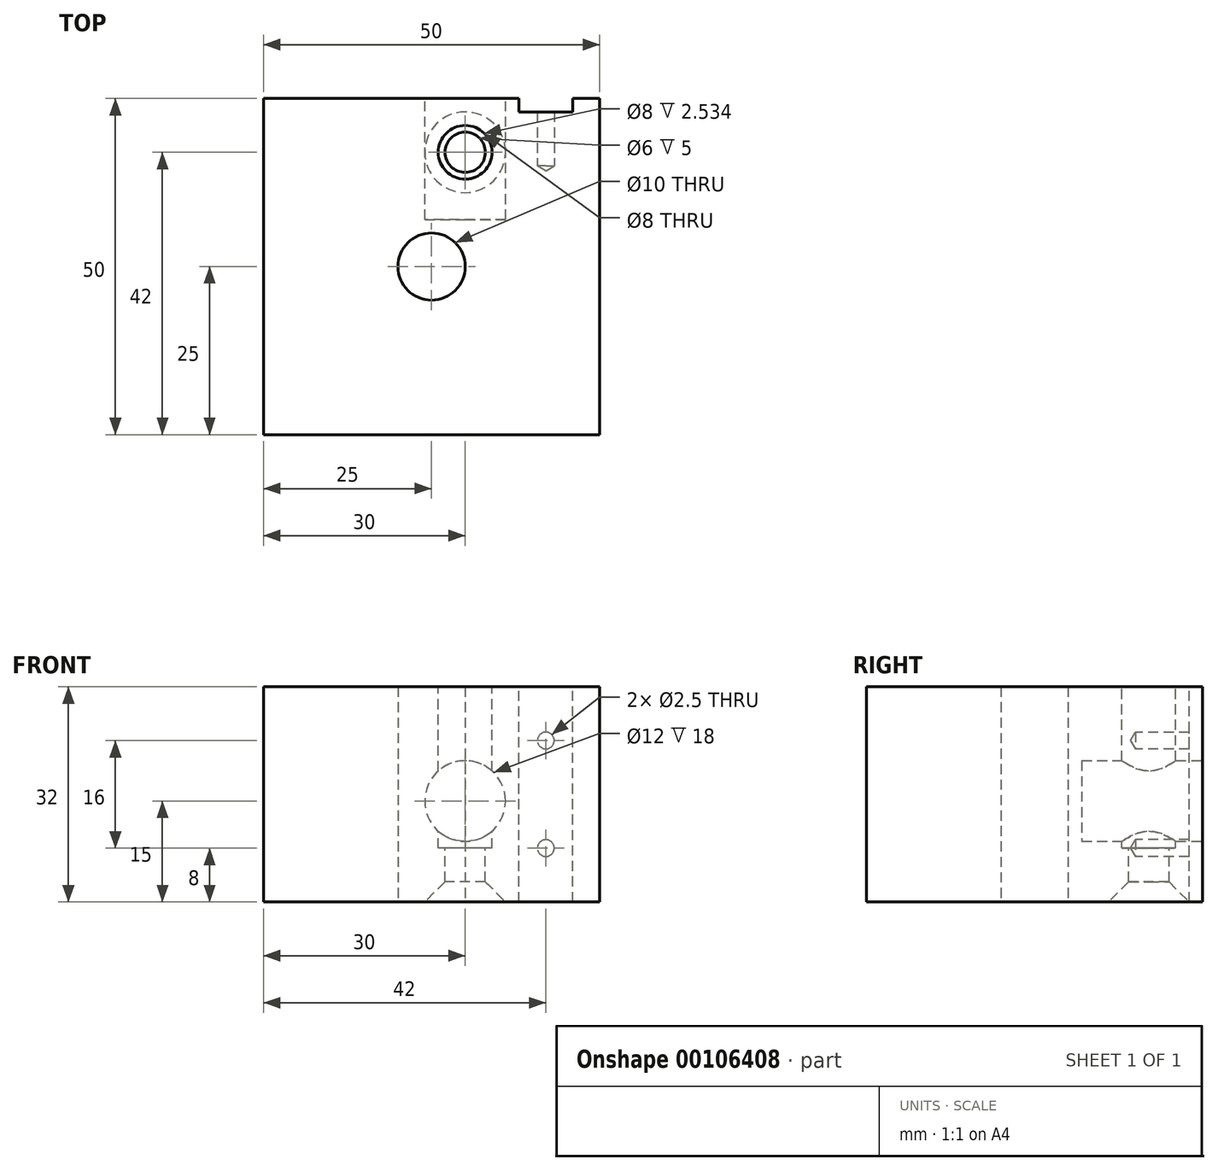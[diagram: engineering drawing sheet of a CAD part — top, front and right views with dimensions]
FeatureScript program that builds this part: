
annotation { "Feature Type Name" : "Feature", "Feature Type Description" : "" }
export const myFeature = defineFeature(function(context is Context, id is Id, definition is map)
    precondition{}
    {
        {
            var Q0;
            Q0=qCreatedBy(makeId("Top.planeOp"),FACE);
            var sketch = newSketch(context, id + "F0", { "sketchPlane" : qUnion([Q0])});
            skLineSegment(sketch, "E0.bottom", {"start": v(25, -25) * mm, "end": v(-25, -25) * mm});
            skLineSegment(sketch, "E0.top", {"start": v(25, 25) * mm, "end": v(-25, 25) * mm});
            skLineSegment(sketch, "E0.left", {"start": v(25, -25) * mm, "end": v(25, 25) * mm});
            skLineSegment(sketch, "E0.right", {"start": v(-25, -25) * mm, "end": v(-25, 25) * mm});
            skPoint(sketch, "E0.middle", {"position": v(0, 0) * mm});
            skCircle(sketch, "E1", {"center": v(0, 0) * mm, "radius": 5 * mm});
            skSolve(sketch);
        }
        {
            var Q0;
            Q0=makeQuery(id+"F0.imprint","IMPRINT",FACE,{"disambiguationData":[TD([[makeQuery(id+"F0.imprint","IMPRINT",EDGE,{"derivedFrom":sQuery(id+"F0.wireOp",EDGE,"E0.bottom")}),-1.0]])]});
            extrude(context, id + "F1", {"entities" : qUnion([Q0]), "depth" : 32 * mm, "symmetric" : true});
        }
        {
            var Q0;
            Q0=makeQuery(id+"F1.opExtrude","CAP_FACE",FACE,{"disambiguationData":[OSD([sQuery(id+"F0.wireOp",EDGE,"E0.bottom"),sQuery(id+"F0.wireOp",EDGE,"E0.top"),sQuery(id+"F0.wireOp",EDGE,"E0.left"),sQuery(id+"F0.wireOp",EDGE,"E0.right"),sQuery(id+"F0.wireOp",EDGE,"E1")])],"isStart":false});
            var sketch = newSketch(context, id + "F2", { "sketchPlane" : qUnion([Q0])});
            skLineSegment(sketch, "E2.bottom", {"start": v(13, 25) * mm, "end": v(21, 25) * mm});
            skLineSegment(sketch, "E2.top", {"start": v(13, 23) * mm, "end": v(21, 23) * mm});
            skLineSegment(sketch, "E2.left", {"start": v(13, 25) * mm, "end": v(13, 23) * mm});
            skLineSegment(sketch, "E2.right", {"start": v(21, 25) * mm, "end": v(21, 23) * mm});
            skSolve(sketch);
        }
        {
            var Q0;
            Q0=makeQuery(id+"F2.imprint","IMPRINT",FACE,{"disambiguationData":[TD([[makeQuery(id+"F2.imprint","IMPRINT",EDGE,{"derivedFrom":sQuery(id+"F2.wireOp",EDGE,"E2.bottom")}),1.0]])]});
            extrude(context, id + "F3", {"entities" : qUnion([Q0]), "operationType" : NewBodyOperationType.REMOVE, "endBound" : BoundingType.THROUGH_ALL, "oppositeDirection" : true, "depth" : 25 * mm});
        }
        {
            var Q0;
            Q0=makeQuery(id+"F1.opExtrude","CAP_FACE",FACE,{"disambiguationData":[OSD([sQuery(id+"F0.wireOp",EDGE,"E0.bottom"),sQuery(id+"F0.wireOp",EDGE,"E0.top"),sQuery(id+"F0.wireOp",EDGE,"E0.left"),sQuery(id+"F0.wireOp",EDGE,"E0.right"),sQuery(id+"F0.wireOp",EDGE,"E1")])],"isStart":false});
            var sketch = newSketch(context, id + "F4", { "sketchPlane" : qUnion([Q0])});
            skCircle(sketch, "E3", {"center": v(5, 17) * mm, "radius": 3 * mm});
            skSolve(sketch);
        }
        {
            var Q0;
            Q0=makeQuery(id+"F4.imprint","IMPRINT",FACE,{"disambiguationData":[TD([[makeQuery(id+"F4.imprint","IMPRINT",EDGE,{"derivedFrom":sQuery(id+"F4.wireOp",EDGE,"E3")}),1.0]])]});
            extrude(context, id + "F5", {"entities" : qUnion([Q0]), "operationType" : NewBodyOperationType.REMOVE, "endBound" : BoundingType.THROUGH_ALL, "oppositeDirection" : true, "depth" : 25 * mm});
        }
        {
            var Q0;
            Q0=makeQuery(id+"F1.opExtrude","CAP_FACE",FACE,{"disambiguationData":[OSD([sQuery(id+"F0.wireOp",EDGE,"E0.bottom"),sQuery(id+"F0.wireOp",EDGE,"E0.top"),sQuery(id+"F0.wireOp",EDGE,"E0.left"),sQuery(id+"F0.wireOp",EDGE,"E0.right"),sQuery(id+"F0.wireOp",EDGE,"E1")])],"isStart":false});
            var sketch = newSketch(context, id + "F6", { "sketchPlane" : qUnion([Q0])});
            skCircle(sketch, "E4", {"center": v(5, 17) * mm, "radius": 4 * mm});
            skSolve(sketch);
        }
        {
            var Q0;
            Q0=makeQuery(id+"F6.imprint","IMPRINT",FACE,{"disambiguationData":[TD([[makeQuery(id+"F6.imprint","IMPRINT",EDGE,{"derivedFrom":sQuery(id+"F6.wireOp",EDGE,"E4")}),1.0]])]});
            extrude(context, id + "F7", {"entities" : qUnion([Q0]), "operationType" : NewBodyOperationType.REMOVE, "oppositeDirection" : true, "depth" : 24 * mm});
        }
        {
            var Q0;
            {var subQ1=sQuery(id+"F0.wireOp",EDGE,"E0.right");var subQ3=sQuery(id+"F0.wireOp",EDGE,"E0.top");Q0=makeQuery(id+"F3.boolean.opBoolean","SPLIT",FACE,{"disambiguationData":[TD([makeQuery(id+"F1.opExtrude","SWEPT_FACE",FACE,{"disambiguationData":[OSD([subQ1])]})])],"derivedFrom":makeQuery(id+"F1.opExtrude","SWEPT_FACE",FACE,{"disambiguationData":[OSD([subQ3])]})});}
            var sketch = newSketch(context, id + "F8", { "sketchPlane" : qUnion([Q0])});
            skCircle(sketch, "E5", {"center": v(-5, -1) * mm, "radius": 6 * mm});
            skSolve(sketch);
        }
        {
            var Q0;
            Q0=makeQuery(id+"F8.imprint","IMPRINT",FACE,{"disambiguationData":[TD([[makeQuery(id+"F8.imprint","IMPRINT",EDGE,{"derivedFrom":sQuery(id+"F8.wireOp",EDGE,"E5")}),1.0]])]});
            extrude(context, id + "F9", {"entities" : qUnion([Q0]), "operationType" : NewBodyOperationType.REMOVE, "oppositeDirection" : true, "depth" : 18 * mm});
        }
        {
            var Q0;
            Q0=makeQuery(id+"F5.boolean.opBoolean","INTERSECT",EDGE,{"derivedFrom":[makeQuery(id+"F1.opExtrude","CAP_FACE",FACE,{"disambiguationData":[OSD([sQuery(id+"F0.wireOp",EDGE,"E0.bottom"),sQuery(id+"F0.wireOp",EDGE,"E0.top"),sQuery(id+"F0.wireOp",EDGE,"E0.left"),sQuery(id+"F0.wireOp",EDGE,"E0.right"),sQuery(id+"F0.wireOp",EDGE,"E1")])],"isStart":true}),makeQuery(id+"F5.opExtrude","SWEPT_FACE",FACE,{"disambiguationData":[OSD([sQuery(id+"F4.wireOp",EDGE,"E3")])]})]});
            chamfer(context, id + "F10", {"entities" : qUnion([Q0]), "chamferType" : ChamferType.OFFSET_ANGLE, "width" : 3 * mm, "oppositeDirection" : false, "angle" : 45 * degree, "tangentPropagation" : true});
        }
        {
            var Q0;
            Q0=makeQuery(id+"F3.boolean.opBoolean","COPY",FACE,{"derivedFrom":makeQuery(id+"F3.opExtrude","SWEPT_FACE",FACE,{"disambiguationData":[OSD([sQuery(id+"F2.wireOp",EDGE,"E2.top")])]})});
            var sketch = newSketch(context, id + "F11", { "sketchPlane" : qUnion([Q0])});
            skPoint(sketch, "E6", {"position": v(-17, 8) * mm});
            skPoint(sketch, "E7", {"position": v(-17, -8) * mm});
            skLineSegment(sketch, "E8", {"start": v(-17, 16) * mm, "end": v(-17, -16) * mm, "construction": true});
            skSolve(sketch);
        }
        {
            var Q0;
            Q0=sQuery(id+"F11.wireOp",VERTEX,"E6");
            var Q1;
            Q1=sQuery(id+"F11.wireOp",VERTEX,"E7");
            var Q2;
            Q2=makeQuery(id+"F1.opExtrude","SWEPT_BODY",BODY,{"disambiguationData":[OSD([sQuery(id+"F0.wireOp",EDGE,"E0.bottom"),sQuery(id+"F0.wireOp",EDGE,"E0.top"),sQuery(id+"F0.wireOp",EDGE,"E0.left"),sQuery(id+"F0.wireOp",EDGE,"E0.right"),sQuery(id+"F0.wireOp",EDGE,"E1")])]});
            hole(context, id + "F12", {"style" : HoleStyle.SIMPLE, "endStyle" : HoleEndStyle.BLIND, "standardTappedOrClearance" : lookupTablePath({ "standard" : "ISO", "engagement" : "75%", "pitch" : "0.5 mm", "size" : "M3", "type" : "Tapped" }), "standardBlindInLast" : lookupTablePath({ "standard" : "ISO", "engagement" : "75%", "pitch" : "0.5 mm", "size" : "M3", "type" : "Tapped" }), "holeDiameter" : 2.5 * mm, "holeDepth" : 8 * mm, "locations" : qUnion([Q0, Q1]), "scope" : qUnion([Q2]), "majorDiameter" : 3 * mm, "startStyle" : HoleStartStyle.SKETCH});
        }
    });
